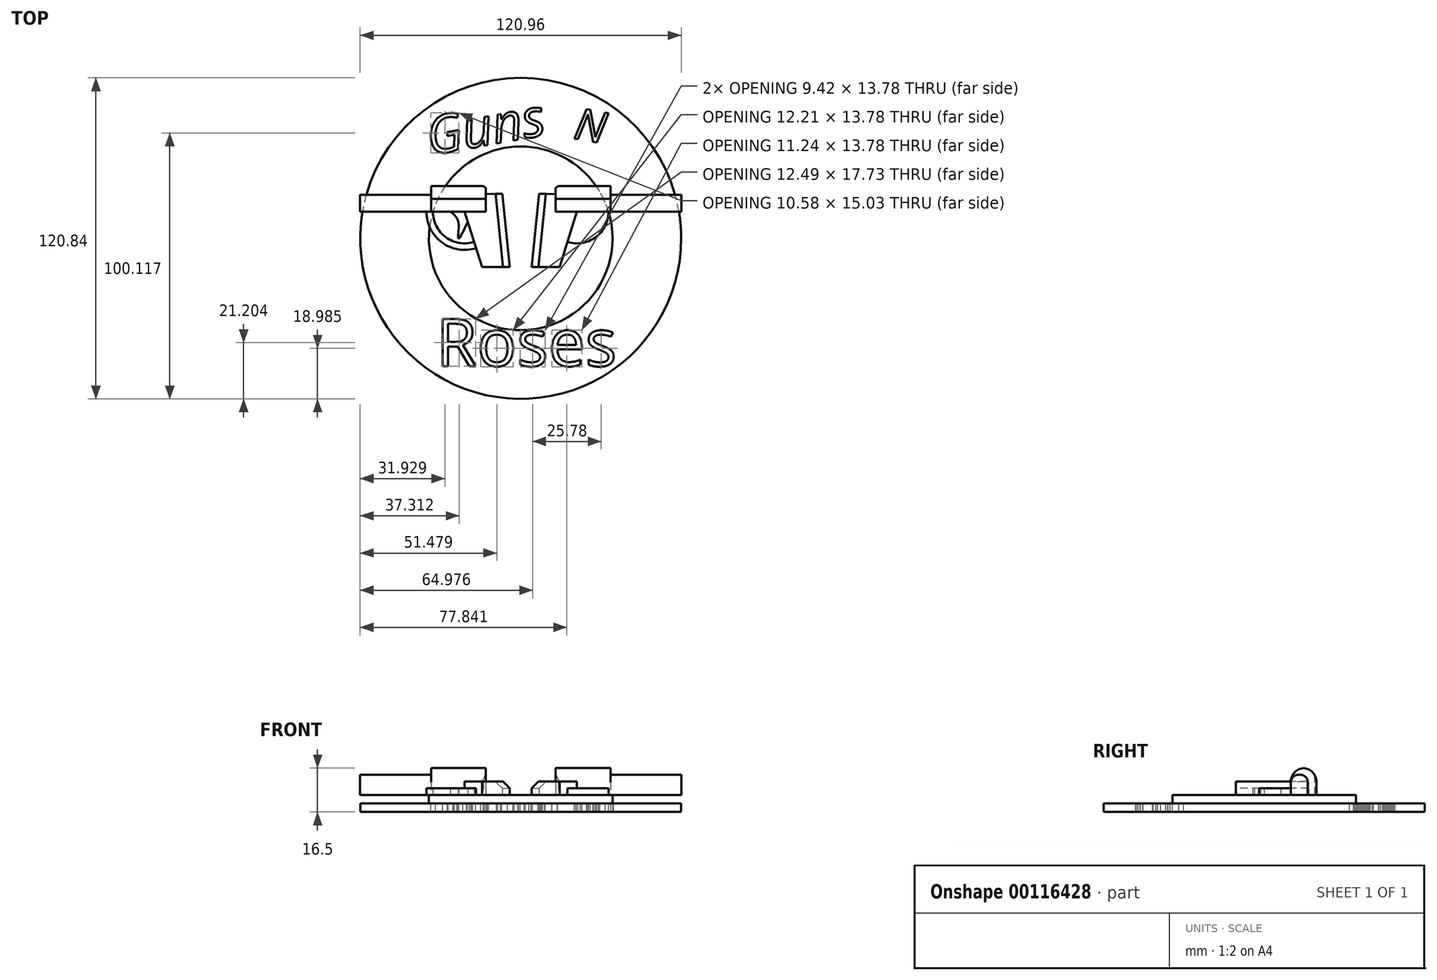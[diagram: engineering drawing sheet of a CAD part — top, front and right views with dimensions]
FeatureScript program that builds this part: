
annotation { "Feature Type Name" : "Feature", "Feature Type Description" : "" }
export const myFeature = defineFeature(function(context is Context, id is Id, definition is map)
    precondition{}
    {
        {
            var Q0;
            Q0=qCreatedBy(makeId("Top.planeOp"),FACE);
            var sketch = newSketch(context, id + "F0", { "sketchPlane" : qUnion([Q0])});
            skCircle(sketch, "E0", {"center": v(0, 0) * mm, "radius": 34.58 * mm});
            skCircle(sketch, "E1", {"center": v(0, 0) * mm, "radius": 60.42 * mm});
            skSolve(sketch);
        }
        {
            var Q0;
            Q0=makeQuery(id+"F0.imprint","IMPRINT",FACE,{"disambiguationData":[TD([[makeQuery(id+"F0.imprint","IMPRINT",EDGE,{"derivedFrom":sQuery(id+"F0.wireOp",EDGE,"E0")}),1.0]])]});
            extrude(context, id + "F1", {"entities" : qUnion([Q0]), "depth" : 6.35 * mm});
        }
        {
            var Q0;
            Q0=makeQuery(id+"F0.imprint","IMPRINT",FACE,{"disambiguationData":[TD([[makeQuery(id+"F0.imprint","IMPRINT",EDGE,{"derivedFrom":sQuery(id+"F0.wireOp",EDGE,"E0")}),-1.0]])]});
            extrude(context, id + "F2", {"entities" : qUnion([Q0]), "operationType" : NewBodyOperationType.ADD, "depth" : 3.17 * mm});
        }
        {
            var Q0;
            Q0=makeQuery(id+"F2.opExtrude","CAP_FACE",FACE,{"disambiguationData":[OSD([sQuery(id+"F0.wireOp",EDGE,"E0"),sQuery(id+"F0.wireOp",EDGE,"E1")])],"isStart":false});
            var sketch = newSketch(context, id + "F3", { "sketchPlane" : qUnion([Q0])});
            skText(sketch, "E2", { "text": "N", "fontName": "OpenSans-Italic.ttf"});
            skText(sketch, "E3", { "text": "Guns", "fontName": "OpenSans-Italic.ttf"});
            skText(sketch, "E4", { "text": "Roses", "fontName": "OpenSans-Regular.ttf"});
            const initialGuessF3  = {"E2": [0.01962, 0.03765, 0.9848, -0.17365, 0.01185], "E3": [-0.03419, 0.03131, 0.9848, 0.17365, 0.01429], "E4": [-0.03185, -0.04808, 1, 0, 0.01788]};
            skSetInitialGuess(sketch, initialGuessF3);
            skSolve(sketch);
        }
        {
            var Q0;
            Q0 = qSketchRegion(id + "F3", true);
            extrude(context, id + "F4", {"entities" : qUnion([Q0]), "operationType" : NewBodyOperationType.REMOVE, "oppositeDirection" : true, "depth" : 25.4 * mm});
        }
        {
            var Q0;
            Q0=makeQuery(id+"F1.opExtrude","CAP_FACE",FACE,{"disambiguationData":[OSD([sQuery(id+"F0.wireOp",EDGE,"E0")])],"isStart":false});
            var sketch = newSketch(context, id + "F5", { "sketchPlane" : qUnion([Q0])});
            skLineSegment(sketch, "E5.bottom", {"start": v(-60.48, 16.45) * mm, "end": v(-33.8, 16.45) * mm});
            skLineSegment(sketch, "E5.top", {"start": v(-60.48, 10.06) * mm, "end": v(-21.13, 10.06) * mm});
            skLineSegment(sketch, "E5.left", {"start": v(-60.48, 16.45) * mm, "end": v(-60.48, 10.06) * mm});
            skLineSegment(sketch, "E6", {"start": v(-21.13, 10.06) * mm, "end": v(-14.6, -10.7) * mm});
            skLineSegment(sketch, "E7", {"start": v(-14.6, -10.7) * mm, "end": v(-4.1, -10.7) * mm});
            skLineSegment(sketch, "E8", {"start": v(-13.18, 16.66) * mm, "end": v(-6.96, 16.82) * mm});
            skLineSegment(sketch, "E9.bottom", {"start": v(-33.8, 19.7) * mm, "end": v(-13.18, 19.7) * mm});
            skLineSegment(sketch, "E9.top", {"start": v(-33.8, 10.06) * mm, "end": v(-21.13, 10.06) * mm});
            skLineSegment(sketch, "E9.left", {"start": v(-33.8, 19.7) * mm, "end": v(-33.8, 10.06) * mm});
            skLineSegment(sketch, "E9.right", {"start": v(-13.18, 19.7) * mm, "end": v(-13.18, 16.66) * mm});
            skLineSegment(sketch, "E10", {"start": v(-6.96, 16.82) * mm, "end": v(-4.1, -10.7) * mm});
            skArc(sketch, "E11", {"start": v(-13.18, 18.96) * mm, "mid": v(-13.63, 19.34) * mm, "end": v(-14.1, 19.7) * mm});
            skPoint(sketch, "E12.1.internal.snap0", {"position": v(-23.49, 10.06) * mm});
            skPoint(sketch, "E12.2.internal.snap0", {"position": v(-23.49, 10.06) * mm});
            skFitSpline(sketch, "E12", {"points": [v(-26.52, 10.06) * mm, v(-23.49, 6.06) * mm, v(-23.49, 0) * mm, v(-19.93, 6.23) * mm], "startDerivative": vector(13.12, -9.75) * mm, "endDerivative": vector(13.27, 27.34) * mm});
            skPoint(sketch, "E13.orphan", {"position": v(-13.18, 10.06) * mm});
            skArc(sketch, "E14.trimOffspring", {"start": v(-33.06, 10.06) * mm, "mid": v(-28.2, 0.44) * mm, "end": v(-17.55, -1.32) * mm});
            skLineSegment(sketch, "E15", {"start": v(-13.18, 16.66) * mm, "end": v(-13.18, 10.06) * mm});
            skLineSegment(sketch, "E16", {"start": v(-21.13, 10.06) * mm, "end": v(-13.18, 10.06) * mm});
            skArc(sketch, "E17", {"start": v(-33.8, 16.89) * mm, "mid": v(-33.9, 16.67) * mm, "end": v(-34.02, 16.45) * mm});
            skArc(sketch, "E18.trimOffspring", {"start": v(-35.52, 10.06) * mm, "mid": v(-29.64, -1.54) * mm, "end": v(-16.82, -3.66) * mm});
            skLineSegment(sketch, "E19", {"start": v(0, 34.58) * mm, "end": v(0, -34.58) * mm, "construction": true});
            skArc(sketch, "E20.MirrorCS", {"start": v(33.8, 16.89) * mm, "mid": v(33.9, 16.67) * mm, "end": v(34.02, 16.45) * mm});
            skLineSegment(sketch, "E21.MirrorCS", {"start": v(13.18, 16.66) * mm, "end": v(13.18, 10.06) * mm});
            skArc(sketch, "E22.MirrorCS", {"start": v(13.18, 18.96) * mm, "mid": v(13.63, 19.34) * mm, "end": v(14.1, 19.7) * mm});
            skLineSegment(sketch, "E23.MirrorCS", {"start": v(13.18, 19.7) * mm, "end": v(13.18, 16.66) * mm});
            skLineSegment(sketch, "E24.MirrorCS", {"start": v(33.8, 19.7) * mm, "end": v(33.8, 10.06) * mm});
            skLineSegment(sketch, "E25.MirrorCS", {"start": v(60.48, 16.45) * mm, "end": v(60.48, 10.06) * mm});
            skLineSegment(sketch, "E26.MirrorCS", {"start": v(33.8, 10.06) * mm, "end": v(21.13, 10.06) * mm});
            skLineSegment(sketch, "E27.MirrorCS", {"start": v(13.18, 16.66) * mm, "end": v(6.96, 16.82) * mm});
            skPoint(sketch, "E28.MirrorP", {"position": v(23.49, 10.06) * mm});
            skLineSegment(sketch, "E29.MirrorCS", {"start": v(21.13, 10.06) * mm, "end": v(13.18, 10.06) * mm});
            skLineSegment(sketch, "E30.MirrorCS", {"start": v(21.13, 10.06) * mm, "end": v(14.6, -10.7) * mm});
            skFitSpline(sketch, "E31.MirrorCS", {"points": [v(26.52, 10.06) * mm, v(23.49, 6.06) * mm, v(23.49, 0) * mm, v(19.93, 6.23) * mm], "startDerivative": vector(-13.12, -9.75) * mm, "endDerivative": vector(-13.27, 27.34) * mm});
            skArc(sketch, "E32.MirrorCS", {"start": v(35.52, 10.06) * mm, "mid": v(29.64, -1.54) * mm, "end": v(16.82, -3.66) * mm});
            skArc(sketch, "E33.MirrorCS", {"start": v(33.06, 10.06) * mm, "mid": v(28.2, 0.44) * mm, "end": v(17.55, -1.32) * mm});
            skLineSegment(sketch, "E34.MirrorCS", {"start": v(60.48, 16.45) * mm, "end": v(33.8, 16.45) * mm});
            skLineSegment(sketch, "E35.MirrorCS", {"start": v(6.96, 16.82) * mm, "end": v(4.1, -10.7) * mm});
            skLineSegment(sketch, "E36.MirrorCS", {"start": v(60.48, 10.06) * mm, "end": v(21.13, 10.06) * mm});
            skLineSegment(sketch, "E37.MirrorCS", {"start": v(33.8, 19.7) * mm, "end": v(13.18, 19.7) * mm});
            skLineSegment(sketch, "E38.MirrorCS", {"start": v(14.6, -10.7) * mm, "end": v(4.1, -10.7) * mm});
            skPoint(sketch, "E39.MirrorP", {"position": v(13.18, 10.06) * mm});
            skSolve(sketch);
        }
        {
            var Q0;
            {var subQ5=sQuery(id+"F5.wireOp",EDGE,"E14.trimOffspring");Q0=makeQuery(id+"F5.imprint","IMPRINT",FACE,{"disambiguationData":[TD([[makeQuery(id+"F5.imprint","IMPRINT",EDGE,{"derivedFrom":subQ5}),-1.0]])]});}
            var Q1;
            {var subQ1=sQuery(id+"F5.wireOp",EDGE,"E5.top");var subQ3=sQuery(id+"F5.wireOp",EDGE,"E18.trimOffspring");var subQ4=makeQuery(id+"F5.imprint","INTERSECT",VERTEX,{"derivedFrom":[subQ1,subQ3]});Q1=makeQuery(id+"F5.imprint","IMPRINT",FACE,{"disambiguationData":[TD([[makeQuery(id+"F5.imprint","IMPRINT",EDGE,{"disambiguationData":[TD([[subQ4,-1.0]])],"derivedFrom":subQ3}),1.0]])]});}
            var Q2;
            {var subQ3=sQuery(id+"F5.wireOp",EDGE,"E12");Q2=makeQuery(id+"F5.imprint","IMPRINT",FACE,{"disambiguationData":[TD([[makeQuery(id+"F5.imprint","IMPRINT",EDGE,{"derivedFrom":subQ3}),1.0]])]});}
            var Q3;
            {var subQ3=sQuery(id+"F5.wireOp",EDGE,"E31.MirrorCS");Q3=makeQuery(id+"F5.imprint","IMPRINT",FACE,{"disambiguationData":[TD([[makeQuery(id+"F5.imprint","IMPRINT",EDGE,{"derivedFrom":subQ3}),-1.0]])]});}
            var Q4;
            {var subQ1=sQuery(id+"F5.wireOp",EDGE,"E33.MirrorCS");Q4=makeQuery(id+"F5.imprint","IMPRINT",FACE,{"disambiguationData":[TD([[makeQuery(id+"F5.imprint","IMPRINT",EDGE,{"derivedFrom":subQ1}),1.0]])]});}
            var Q5;
            {var subQ0=sQuery(id+"F5.wireOp",EDGE,"E36.MirrorCS");var subQ1=sQuery(id+"F5.wireOp",EDGE,"E32.MirrorCS");var subQ2=makeQuery(id+"F5.imprint","INTERSECT",VERTEX,{"derivedFrom":[subQ1,subQ0]});Q5=makeQuery(id+"F5.imprint","IMPRINT",FACE,{"disambiguationData":[TD([[makeQuery(id+"F5.imprint","IMPRINT",EDGE,{"disambiguationData":[TD([[subQ2,-1.0]])],"derivedFrom":subQ1}),-1.0]])]});}
            extrude(context, id + "F6", {"entities" : qUnion([Q0, Q1, Q2, Q3, Q4, Q5]), "operationType" : NewBodyOperationType.ADD, "depth" : 2.54 * mm});
        }
        {
            var Q0;
            {var subQ0=sQuery(id+"F5.wireOp",EDGE,"E7");Q0=makeQuery(id+"F5.imprint","IMPRINT",FACE,{"disambiguationData":[TD([[makeQuery(id+"F5.imprint","IMPRINT",EDGE,{"derivedFrom":subQ0}),1.0]])]});}
            var Q1;
            Q1=makeQuery(id+"F5.imprint","IMPRINT",FACE,{"disambiguationData":[TD([[makeQuery(id+"F5.imprint","IMPRINT",EDGE,{"derivedFrom":sQuery(id+"F5.wireOp",EDGE,"E21.MirrorCS")}),-1.0]])]});
            extrude(context, id + "F7", {"entities" : qUnion([Q0, Q1]), "operationType" : NewBodyOperationType.ADD, "depth" : 5.08 * mm});
        }
        {
            var Q0;
            {var subQ4=sQuery(id+"F5.wireOp",EDGE,"E5.left");Q0=makeQuery(id+"F5.imprint","IMPRINT",FACE,{"disambiguationData":[TD([[makeQuery(id+"F5.imprint","IMPRINT",EDGE,{"derivedFrom":subQ4}),1.0]])]});}
            var Q1;
            {var subQ4=sQuery(id+"F5.wireOp",EDGE,"E25.MirrorCS");Q1=makeQuery(id+"F5.imprint","IMPRINT",FACE,{"disambiguationData":[TD([[makeQuery(id+"F5.imprint","IMPRINT",EDGE,{"derivedFrom":subQ4}),-1.0]])]});}
            extrude(context, id + "F8", {"entities" : qUnion([Q0, Q1]), "operationType" : NewBodyOperationType.ADD, "depth" : 7.62 * mm});
        }
        {
            var Q0;
            {var subQ3=sQuery(id+"F5.wireOp",EDGE,"E11");Q0=makeQuery(id+"F5.imprint","IMPRINT",FACE,{"disambiguationData":[TD([[makeQuery(id+"F5.imprint","IMPRINT",EDGE,{"derivedFrom":subQ3}),1.0]])]});}
            var Q1;
            {var subQ2=sQuery(id+"F5.wireOp",EDGE,"E21.MirrorCS");Q1=makeQuery(id+"F5.imprint","IMPRINT",FACE,{"disambiguationData":[TD([[makeQuery(id+"F5.imprint","IMPRINT",EDGE,{"derivedFrom":subQ2}),1.0]])]});}
            var Q2;
            {var subQ1=sQuery(id+"F5.wireOp",EDGE,"E24.MirrorCS");var subQ9=makeQuery(id+"F5.imprint","INTERSECT",VERTEX,{"derivedFrom":[sQuery(id+"F5.wireOp",EDGE,"E20.MirrorCS"),subQ1]});Q2=makeQuery(id+"F5.imprint","IMPRINT",FACE,{"disambiguationData":[TD([[makeQuery(id+"F5.imprint","IMPRINT",EDGE,{"disambiguationData":[TD([[subQ9,1.0]])],"derivedFrom":subQ1}),-1.0]])]});}
            var Q3;
            {var subQ0=sQuery(id+"F5.wireOp",EDGE,"E9.left");var subQ3=sQuery(id+"F5.wireOp",EDGE,"E9.bottom");var subQ4=makeQuery(id+"F5.imprint","INTERSECT",VERTEX,{"derivedFrom":[subQ3,subQ0]});Q3=makeQuery(id+"F5.imprint","IMPRINT",FACE,{"disambiguationData":[TD([[makeQuery(id+"F5.imprint","IMPRINT",EDGE,{"disambiguationData":[TD([[subQ4,-1.0]])],"derivedFrom":subQ3}),-1.0]])]});}
            extrude(context, id + "F9", {"entities" : qUnion([Q0, Q1, Q2, Q3]), "operationType" : NewBodyOperationType.ADD, "depth" : 10.16 * mm});
        }
        {
            var Q0;
            Q0=makeQuery(id+"F8.opExtrude","CAP_EDGE",EDGE,{"disambiguationData":[OSD([sQuery(id+"F5.wireOp",EDGE,"E5.bottom")])],"isStart":false});
            var Q1;
            Q1=makeQuery(id+"F8.opExtrude","CAP_EDGE",EDGE,{"disambiguationData":[OSD([sQuery(id+"F5.wireOp",EDGE,"E5.top")])],"isStart":false});
            var Q2;
            Q2=makeQuery(id+"F8.opExtrude","CAP_EDGE",EDGE,{"disambiguationData":[OSD([sQuery(id+"F5.wireOp",EDGE,"E34.MirrorCS")])],"isStart":false});
            var Q3;
            Q3=makeQuery(id+"F8.opExtrude","CAP_EDGE",EDGE,{"disambiguationData":[OSD([sQuery(id+"F5.wireOp",EDGE,"E36.MirrorCS")])],"isStart":false});
            fillet(context, id + "F10", {"entities" : qUnion([Q0, Q1, Q2, Q3]), "radius" : 2.8 * mm, "tangentPropagation" : true, "allowEdgeOverflow" : false});
        }
        {
            var Q0;
            Q0=makeQuery(id+"F9.opExtrude","CAP_EDGE",EDGE,{"disambiguationData":[OSD([sQuery(id+"F5.wireOp",EDGE,"E9.bottom")])],"isStart":false});
            var Q1;
            Q1=makeQuery(id+"F9.opExtrude","CAP_EDGE",EDGE,{"disambiguationData":[OSD([sQuery(id+"F5.wireOp",EDGE,"E9.top"),sQuery(id+"F5.wireOp",EDGE,"E16")])],"isStart":false});
            var Q2;
            Q2=makeQuery(id+"F9.opExtrude","CAP_EDGE",EDGE,{"disambiguationData":[OSD([sQuery(id+"F5.wireOp",EDGE,"E37.MirrorCS")])],"isStart":false});
            var Q3;
            Q3=makeQuery(id+"F9.opExtrude","CAP_EDGE",EDGE,{"disambiguationData":[OSD([sQuery(id+"F5.wireOp",EDGE,"E29.MirrorCS"),sQuery(id+"F5.wireOp",EDGE,"E36.MirrorCS")])],"isStart":false});
            fillet(context, id + "F11", {"entities" : qUnion([Q0, Q1, Q2, Q3]), "radius" : 5.08 * mm, "tangentPropagation" : true, "allowEdgeOverflow" : false});
        }
        {
            var Q0;
            Q0=makeQuery(id+"F7.opExtrude","CAP_EDGE",EDGE,{"disambiguationData":[OSD([sQuery(id+"F5.wireOp",EDGE,"E10")])],"isStart":false});
            var Q1;
            Q1=makeQuery(id+"F7.opExtrude","CAP_EDGE",EDGE,{"disambiguationData":[OSD([sQuery(id+"F5.wireOp",EDGE,"E35.MirrorCS")])],"isStart":false});
            chamfer(context, id + "F12", {"entities" : qUnion([Q0, Q1]), "width" : 2.54 * mm, "tangentPropagation" : true});
        }
    });
